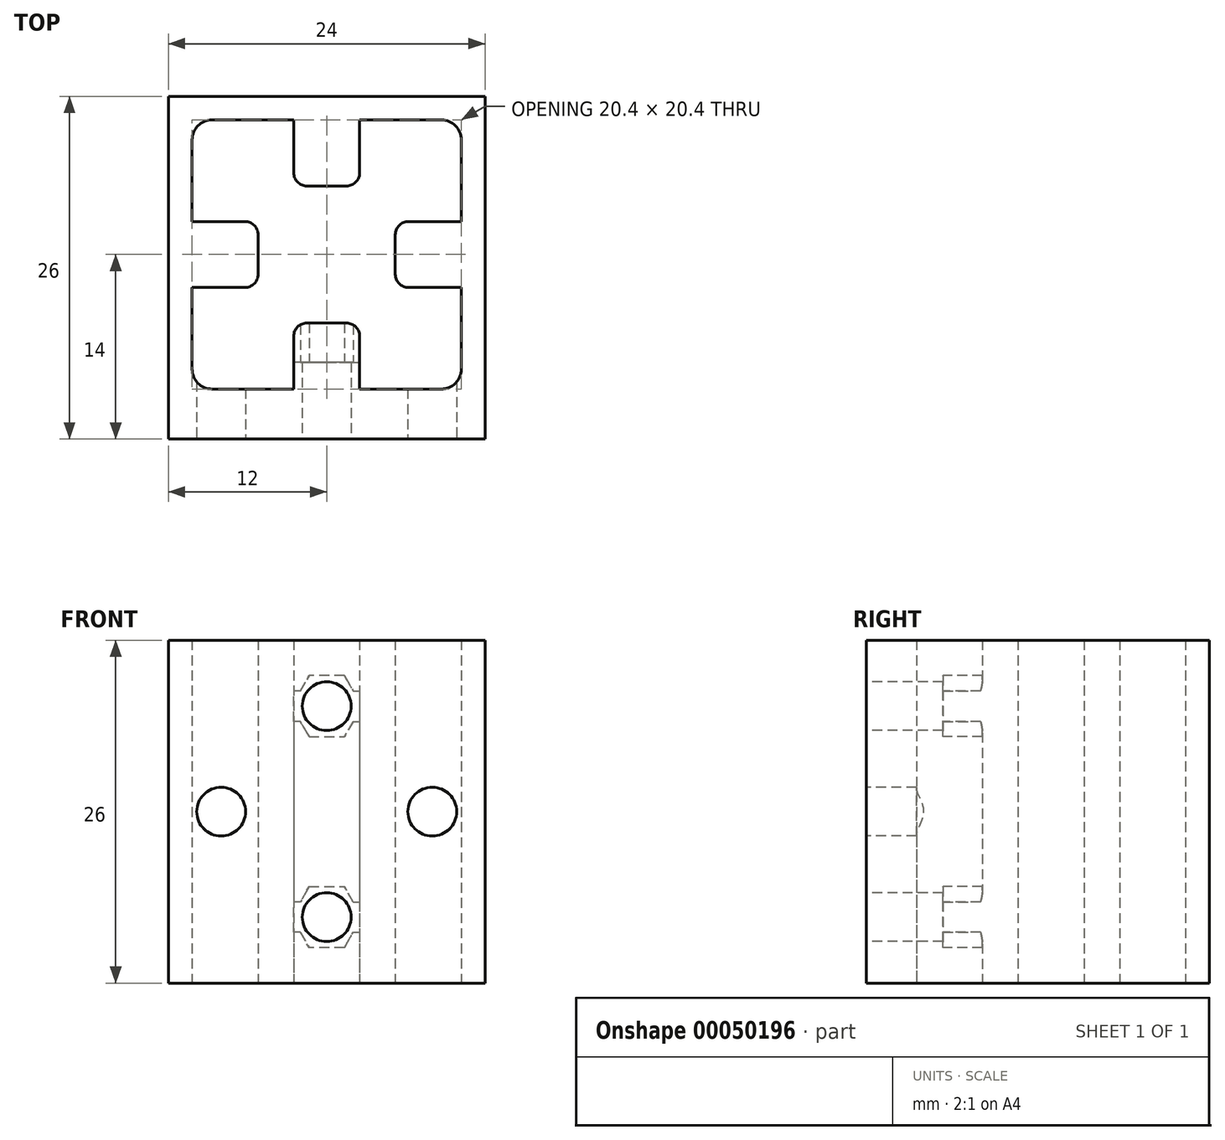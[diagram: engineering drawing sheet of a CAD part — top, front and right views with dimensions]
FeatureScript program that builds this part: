
annotation { "Feature Type Name" : "Feature", "Feature Type Description" : "" }
export const myFeature = defineFeature(function(context is Context, id is Id, definition is map)
    precondition{}
    {
        {
            var Q0;
            Q0=qCreatedBy(makeId("Top.planeOp"),FACE);
            var sketch = newSketch(context, id + "F0", { "sketchPlane" : qUnion([Q0])});
            skLineSegment(sketch, "E0.rect.bottom", {"start": v(-12, -12) * mm, "end": v(12, -12) * mm});
            skLineSegment(sketch, "E0.rect.top", {"start": v(-12, 12) * mm, "end": v(12, 12) * mm});
            skLineSegment(sketch, "E0.rect.left", {"start": v(-12, -12) * mm, "end": v(-12, 12) * mm});
            skLineSegment(sketch, "E0.rect.right", {"start": v(12, -12) * mm, "end": v(12, 12) * mm});
            skLineSegment(sketch, "E1", {"start": v(-10.2, -8.6) * mm, "end": v(-10.2, -2.5) * mm});
            skLineSegment(sketch, "E2.MirrorCS", {"start": v(-10.2, 8.7) * mm, "end": v(-10.2, 2.5) * mm});
            skLineSegment(sketch, "E3", {"start": v(-10.2, 2.5) * mm, "end": v(-6.2, 2.5) * mm});
            skLineSegment(sketch, "E4", {"start": v(-5.2, 1.5) * mm, "end": v(-5.2, -1.5) * mm});
            skLineSegment(sketch, "E5", {"start": v(-6.2, -2.5) * mm, "end": v(-10.2, -2.5) * mm});
            skArc(sketch, "E6.filletArc", {"start": v(-5.2, 1.5) * mm, "mid": v(-5.5, 2.2) * mm, "end": v(-6.2, 2.5) * mm});
            skArc(sketch, "E7.filletArc", {"start": v(-6.2, -2.5) * mm, "mid": v(-5.5, -2.2) * mm, "end": v(-5.2, -1.5) * mm});
            skPoint(sketch, "E8.visualSharp", {"position": v(-10.2, 10.1) * mm});
            skArc(sketch, "E8.filletArc", {"start": v(-8.7, 10.2) * mm, "mid": v(-9.76, 9.76) * mm, "end": v(-10.2, 8.7) * mm});
            skPoint(sketch, "E9.visualSharp", {"position": v(-10.2, -10.1) * mm});
            skPoint(sketch, "E10.1.0", {"position": v(-10.1, -10.2) * mm});
            skPoint(sketch, "E10.3.4", {"position": v(-10.1, 10.2) * mm});
            skLineSegment(sketch, "E11", {"start": v(8.6, -10.2) * mm, "end": v(8.7, -10.2) * mm});
            skLineSegment(sketch, "E12", {"start": v(10.2, 8.7) * mm, "end": v(10.2, 8.6) * mm});
            skLineSegment(sketch, "E13.1.0", {"start": v(-1.5, -5.2) * mm, "end": v(1.5, -5.2) * mm});
            skLineSegment(sketch, "E13.1.1", {"start": v(2.5, -6.2) * mm, "end": v(2.5, -10.2) * mm});
            skLineSegment(sketch, "E13.1.2", {"start": v(-2.5, -10.2) * mm, "end": v(-2.5, -6.2) * mm});
            skLineSegment(sketch, "E13.1.4", {"start": v(-8.7, -10.2) * mm, "end": v(-2.5, -10.2) * mm});
            skLineSegment(sketch, "E13.1.5", {"start": v(8.6, -10.2) * mm, "end": v(2.5, -10.2) * mm});
            skPoint(sketch, "E13.1.6", {"position": v(10.2, -10.1) * mm});
            skPoint(sketch, "E13.1.7", {"position": v(10.1, -10.2) * mm});
            skPoint(sketch, "E13.1.9", {"position": v(10.1, -10.2) * mm});
            skPoint(sketch, "E13.1.11", {"position": v(10.2, -10.1) * mm});
            skArc(sketch, "E13.1.12", {"start": v(2.5, -6.2) * mm, "mid": v(2.2, -5.5) * mm, "end": v(1.5, -5.2) * mm});
            skArc(sketch, "E13.1.13", {"start": v(-1.5, -5.2) * mm, "mid": v(-2.2, -5.5) * mm, "end": v(-2.5, -6.2) * mm});
            skArc(sketch, "E13.1.15", {"start": v(-10.2, -8.7) * mm, "mid": v(-9.76, -9.76) * mm, "end": v(-8.7, -10.2) * mm});
            skLineSegment(sketch, "E13.2.0", {"start": v(5.2, -1.5) * mm, "end": v(5.2, 1.5) * mm});
            skLineSegment(sketch, "E13.2.1", {"start": v(6.2, 2.5) * mm, "end": v(10.2, 2.5) * mm});
            skLineSegment(sketch, "E13.2.2", {"start": v(10.2, -2.5) * mm, "end": v(6.2, -2.5) * mm});
            skPoint(sketch, "E13.2.3", {"position": v(10.1, -10.2) * mm});
            skLineSegment(sketch, "E13.2.4", {"start": v(10.2, -8.7) * mm, "end": v(10.2, -2.5) * mm});
            skLineSegment(sketch, "E13.2.5", {"start": v(10.2, 8.6) * mm, "end": v(10.2, 2.5) * mm});
            skPoint(sketch, "E13.2.6", {"position": v(10.1, 10.2) * mm});
            skPoint(sketch, "E13.2.7", {"position": v(10.2, 10.1) * mm});
            skPoint(sketch, "E13.2.8", {"position": v(10.1, -10.2) * mm});
            skPoint(sketch, "E13.2.9", {"position": v(10.2, 10.1) * mm});
            skPoint(sketch, "E13.2.10", {"position": v(10.2, -10.1) * mm});
            skPoint(sketch, "E13.2.11", {"position": v(10.1, 10.2) * mm});
            skArc(sketch, "E13.2.12", {"start": v(6.2, 2.5) * mm, "mid": v(5.5, 2.2) * mm, "end": v(5.2, 1.5) * mm});
            skArc(sketch, "E13.2.13", {"start": v(5.2, -1.5) * mm, "mid": v(5.5, -2.2) * mm, "end": v(6.2, -2.5) * mm});
            skPoint(sketch, "E13.2.14", {"position": v(10.2, -10.1) * mm});
            skArc(sketch, "E13.2.15", {"start": v(8.7, -10.2) * mm, "mid": v(9.76, -9.76) * mm, "end": v(10.2, -8.7) * mm});
            skLineSegment(sketch, "E13.3.0", {"start": v(1.5, 5.2) * mm, "end": v(-1.5, 5.2) * mm});
            skLineSegment(sketch, "E13.3.1", {"start": v(-2.5, 6.2) * mm, "end": v(-2.5, 10.2) * mm});
            skLineSegment(sketch, "E13.3.2", {"start": v(2.5, 10.2) * mm, "end": v(2.5, 6.2) * mm});
            skPoint(sketch, "E13.3.3", {"position": v(10.2, 10.1) * mm});
            skLineSegment(sketch, "E13.3.4", {"start": v(8.7, 10.2) * mm, "end": v(2.5, 10.2) * mm});
            skLineSegment(sketch, "E13.3.5", {"start": v(-8.6, 10.2) * mm, "end": v(-2.5, 10.2) * mm});
            skPoint(sketch, "E13.3.8", {"position": v(10.2, 10.1) * mm});
            skPoint(sketch, "E13.3.10", {"position": v(10.1, 10.2) * mm});
            skArc(sketch, "E13.3.12", {"start": v(-2.5, 6.2) * mm, "mid": v(-2.2, 5.5) * mm, "end": v(-1.5, 5.2) * mm});
            skArc(sketch, "E13.3.13", {"start": v(1.5, 5.2) * mm, "mid": v(2.2, 5.5) * mm, "end": v(2.5, 6.2) * mm});
            skPoint(sketch, "E13.3.14", {"position": v(10.1, 10.2) * mm});
            skArc(sketch, "E13.3.15", {"start": v(10.2, 8.7) * mm, "mid": v(9.76, 9.76) * mm, "end": v(8.7, 10.2) * mm});
            skPoint(sketch, "E13.center", {"position": v(0, 0) * mm});
            skLineSegment(sketch, "E14", {"start": v(-8.7, 10.2) * mm, "end": v(-8.6, 10.2) * mm});
            skLineSegment(sketch, "E15", {"start": v(-10.2, -8.6) * mm, "end": v(-10.2, -8.7) * mm});
            skSolve(sketch);
        }
        {
            var Q0;
            Q0=makeQuery(id+"F0.imprint","IMPRINT",FACE,{"disambiguationData":[TD([[makeQuery(id+"F0.imprint","IMPRINT",EDGE,{"derivedFrom":sQuery(id+"F0.wireOp",EDGE,"E0.rect.bottom")}),1.0]])]});
            extrude(context, id + "F1", {"entities" : qUnion([Q0]), "depth" : 26 * mm});
        }
        {
            var Q0;
            Q0=makeQuery(id+"F1.opExtrude","SWEPT_FACE",FACE,{"disambiguationData":[OSD([sQuery(id+"F0.wireOp",EDGE,"E0.rect.bottom")])]});
            var sketch = newSketch(context, id + "F2", { "sketchPlane" : qUnion([Q0])});
            skCircle(sketch, "E16", {"center": v(0, 5) * mm, "radius": 1.85 * mm});
            skCircle(sketch, "E17", {"center": v(0, 13) * mm, "radius": 4 * mm});
            skCircle(sketch, "E18.1.0", {"center": v(8, 13) * mm, "radius": 1.85 * mm});
            skCircle(sketch, "E18.2.0", {"center": v(0, 21) * mm, "radius": 1.85 * mm});
            skCircle(sketch, "E18.3.0", {"center": v(-8, 13) * mm, "radius": 1.85 * mm});
            skLineSegment(sketch, "E19", {"start": v(0, 13) * mm, "end": v(8, 13) * mm, "construction": true});
            skLineSegment(sketch, "E20", {"start": v(0, 13) * mm, "end": v(0, 5) * mm, "construction": true});
            skLineSegment(sketch, "E21", {"start": v(0, 5) * mm, "end": v(0, 0) * mm, "construction": true});
            skLineSegment(sketch, "E22.0.1.0", {"start": v(0, 45) * mm, "end": v(8, 45) * mm, "construction": true});
            skCircle(sketch, "E22.0.1.1", {"center": v(-8, 45) * mm, "radius": 1.85 * mm});
            skCircle(sketch, "E22.0.1.2", {"center": v(8, 45) * mm, "radius": 1.85 * mm});
            skCircle(sketch, "E22.0.1.3", {"center": v(0, 37) * mm, "radius": 1.85 * mm});
            skCircle(sketch, "E22.0.1.4", {"center": v(0, 45) * mm, "radius": 4 * mm});
            skPoint(sketch, "E22.0.1.5", {"position": v(0, 45) * mm});
            skLineSegment(sketch, "E22.0.1.6", {"start": v(0, 45) * mm, "end": v(0, 37) * mm, "construction": true});
            skCircle(sketch, "E22.0.1.7", {"center": v(0, 53) * mm, "radius": 1.85 * mm});
            skLineSegment(sketch, "E22.direction2", {"start": v(0, 13) * mm, "end": v(0, 45) * mm, "construction": true});
            skCircle(sketch, "E23", {"center": v(-8, 29) * mm, "radius": 1.85 * mm});
            skPoint(sketch, "E23.centerSnap0", {"position": v(0, 29) * mm});
            skCircle(sketch, "E24.MirrorC", {"center": v(8, 29) * mm, "radius": 1.85 * mm});
            skSolve(sketch);
        }
        {
            var Q0;
            Q0=makeQuery(id+"F2.imprint","IMPRINT",FACE,{"disambiguationData":[TD([[makeQuery(id+"F2.imprint","IMPRINT",EDGE,{"derivedFrom":sQuery(id+"F2.wireOp",EDGE,"E22.0.1.7")}),1.0]])]});
            var Q1;
            Q1=makeQuery(id+"F2.imprint","IMPRINT",FACE,{"disambiguationData":[TD([[makeQuery(id+"F2.imprint","IMPRINT",EDGE,{"derivedFrom":sQuery(id+"F2.wireOp",EDGE,"E22.0.1.2")}),1.0]])]});
            var Q2;
            Q2=makeQuery(id+"F2.imprint","IMPRINT",FACE,{"disambiguationData":[TD([[makeQuery(id+"F2.imprint","IMPRINT",EDGE,{"derivedFrom":sQuery(id+"F2.wireOp",EDGE,"E22.0.1.1")}),1.0]])]});
            var Q3;
            Q3=makeQuery(id+"F2.imprint","IMPRINT",FACE,{"disambiguationData":[TD([[makeQuery(id+"F2.imprint","IMPRINT",EDGE,{"derivedFrom":sQuery(id+"F2.wireOp",EDGE,"E22.0.1.3")}),1.0]])]});
            var Q4;
            Q4=makeQuery(id+"F2.imprint","IMPRINT",FACE,{"disambiguationData":[TD([[makeQuery(id+"F2.imprint","IMPRINT",EDGE,{"derivedFrom":sQuery(id+"F2.wireOp",EDGE,"E23")}),1.0]])]});
            var Q5;
            Q5=makeQuery(id+"F2.imprint","IMPRINT",FACE,{"disambiguationData":[TD([[makeQuery(id+"F2.imprint","IMPRINT",EDGE,{"derivedFrom":sQuery(id+"F2.wireOp",EDGE,"E18.2.0")}),1.0]])]});
            var Q6;
            Q6=makeQuery(id+"F2.imprint","IMPRINT",FACE,{"disambiguationData":[TD([[makeQuery(id+"F2.imprint","IMPRINT",EDGE,{"derivedFrom":sQuery(id+"F2.wireOp",EDGE,"E24.MirrorC")}),-1.0]])]});
            var Q7;
            Q7=makeQuery(id+"F2.imprint","IMPRINT",FACE,{"disambiguationData":[TD([[makeQuery(id+"F2.imprint","IMPRINT",EDGE,{"derivedFrom":sQuery(id+"F2.wireOp",EDGE,"E18.1.0")}),1.0]])]});
            var Q8;
            Q8=makeQuery(id+"F2.imprint","IMPRINT",FACE,{"disambiguationData":[TD([[makeQuery(id+"F2.imprint","IMPRINT",EDGE,{"derivedFrom":sQuery(id+"F2.wireOp",EDGE,"E18.3.0")}),1.0]])]});
            var Q9;
            Q9=makeQuery(id+"F2.imprint","IMPRINT",FACE,{"disambiguationData":[TD([[makeQuery(id+"F2.imprint","IMPRINT",EDGE,{"derivedFrom":sQuery(id+"F2.wireOp",EDGE,"E16")}),1.0]])]});
            extrude(context, id + "F3", {"entities" : qUnion([Q0, Q1, Q2, Q3, Q4, Q5, Q6, Q7, Q8, Q9]), "operationType" : NewBodyOperationType.REMOVE, "oppositeDirection" : true, "depth" : 7.5 * mm});
        }
        {
            var Q0;
            Q0=makeQuery(id+"F1.opExtrude","SWEPT_FACE",FACE,{"disambiguationData":[OSD([sQuery(id+"F0.wireOp",EDGE,"E0.rect.bottom")])]});
            var sketch = newSketch(context, id + "F4", { "sketchPlane" : qUnion([Q0])});
            skCircle(sketch, "E25.cCircle", {"center": v(0, 21) * mm, "radius": 2.3 * mm, "construction": true});
            skLineSegment(sketch, "E25.0", {"start": v(2, 19.84) * mm, "end": v(1.33, 18.7) * mm});
            skLineSegment(sketch, "E25.1", {"start": v(1.33, 18.7) * mm, "end": v(-1.33, 18.7) * mm});
            skLineSegment(sketch, "E25.2", {"start": v(-1.33, 18.7) * mm, "end": v(-2, 19.85) * mm});
            skLineSegment(sketch, "E25.3", {"start": v(-2, 22.15) * mm, "end": v(-1.33, 23.3) * mm});
            skLineSegment(sketch, "E25.4", {"start": v(-1.33, 23.3) * mm, "end": v(1.33, 23.3) * mm});
            skLineSegment(sketch, "E25.5", {"start": v(1.33, 23.3) * mm, "end": v(2, 22.15) * mm});
            skPoint(sketch, "E25.0.midPoint", {"position": v(2, 19.84) * mm});
            skLineSegment(sketch, "E26", {"start": v(-12, 13) * mm, "end": v(12, 13) * mm, "construction": true});
            skLineSegment(sketch, "E27.MirrorCS", {"start": v(2, 6.16) * mm, "end": v(1.33, 7.3) * mm});
            skLineSegment(sketch, "E28.MirrorCS", {"start": v(-1.33, 7.3) * mm, "end": v(-2, 6.15) * mm});
            skLineSegment(sketch, "E29.MirrorCS", {"start": v(-1.33, 2.7) * mm, "end": v(1.33, 2.7) * mm});
            skLineSegment(sketch, "E30.MirrorCS", {"start": v(-2, 3.85) * mm, "end": v(-1.33, 2.7) * mm});
            skLineSegment(sketch, "E31.MirrorCS", {"start": v(1.33, 2.7) * mm, "end": v(2, 3.85) * mm});
            skPoint(sketch, "E32.MirrorP", {"position": v(2, 6.16) * mm});
            skLineSegment(sketch, "E33.MirrorCS", {"start": v(1.33, 7.3) * mm, "end": v(-1.33, 7.3) * mm});
            skCircle(sketch, "E34.MirrorC", {"center": v(0, 5) * mm, "radius": 2.3 * mm, "construction": true});
            skPoint(sketch, "E35.oppositeSnap0", {"position": v(2, 3.85) * mm});
            skLineSegment(sketch, "E35.bottom", {"start": v(2, 6.16) * mm, "end": v(2.67, 6.16) * mm});
            skLineSegment(sketch, "E35.top", {"start": v(2, 3.85) * mm, "end": v(2.67, 3.85) * mm});
            skLineSegment(sketch, "E35.right", {"start": v(2.67, 6.16) * mm, "end": v(2.67, 3.85) * mm});
            skPoint(sketch, "E36.orphan", {"position": v(2.67, 5) * mm});
            skLineSegment(sketch, "E37.MirrorCS", {"start": v(-2.67, 6.16) * mm, "end": v(-2.67, 3.85) * mm});
            skLineSegment(sketch, "E38.MirrorCS", {"start": v(-2, 6.16) * mm, "end": v(-2.67, 6.16) * mm});
            skLineSegment(sketch, "E39.MirrorCS", {"start": v(-2, 3.85) * mm, "end": v(-2.67, 3.85) * mm});
            skPoint(sketch, "E40.orphan", {"position": v(-2.67, 5) * mm});
            skLineSegment(sketch, "E41.MirrorCS", {"start": v(2, 22.15) * mm, "end": v(2.67, 22.15) * mm});
            skLineSegment(sketch, "E42.MirrorCS", {"start": v(2.67, 19.84) * mm, "end": v(2.67, 22.15) * mm});
            skLineSegment(sketch, "E43.MirrorCS", {"start": v(2, 19.84) * mm, "end": v(2.67, 19.84) * mm});
            skLineSegment(sketch, "E44.MirrorCS", {"start": v(-2.67, 19.84) * mm, "end": v(-2.67, 22.15) * mm});
            skLineSegment(sketch, "E45.MirrorCS", {"start": v(-2, 19.84) * mm, "end": v(-2.67, 19.84) * mm});
            skLineSegment(sketch, "E46.MirrorCS", {"start": v(-2, 22.15) * mm, "end": v(-2.67, 22.15) * mm});
            skPoint(sketch, "E47.orphan", {"position": v(2.67, 21) * mm});
            skPoint(sketch, "E48.orphan", {"position": v(-2.67, 21) * mm});
            skSolve(sketch);
        }
        {
            var Q0;
            Q0=makeQuery(id+"F4.imprint","IMPRINT",FACE,{"disambiguationData":[TD([[makeQuery(id+"F4.imprint","IMPRINT",EDGE,{"derivedFrom":sQuery(id+"F4.wireOp",EDGE,"E25.0")}),-1.0]])]});
            var Q1;
            Q1=makeQuery(id+"F4.imprint","IMPRINT",FACE,{"disambiguationData":[TD([[makeQuery(id+"F4.imprint","IMPRINT",EDGE,{"derivedFrom":sQuery(id+"F4.wireOp",EDGE,"E27.MirrorCS")}),1.0]])]});
            extrude(context, id + "F5", {"entities" : qUnion([Q0, Q1]), "operationType" : NewBodyOperationType.REMOVE, "oppositeDirection" : true, "depth" : 7 * mm, "hasSecondDirection" : true, "secondDirectionOppositeDirection" : true, "secondDirectionDepth" : 3.8 * mm});
        }
        {
            var Q0;
            Q0=makeQuery(id+"F1.opExtrude","SWEPT_FACE",FACE,{"disambiguationData":[OSD([sQuery(id+"F0.wireOp",EDGE,"E0.rect.bottom")])]});
            extrude(context, id + "F6", {"entities" : qUnion([Q0]), "operationType" : NewBodyOperationType.ADD, "depth" : 2 * mm});
        }
    });
